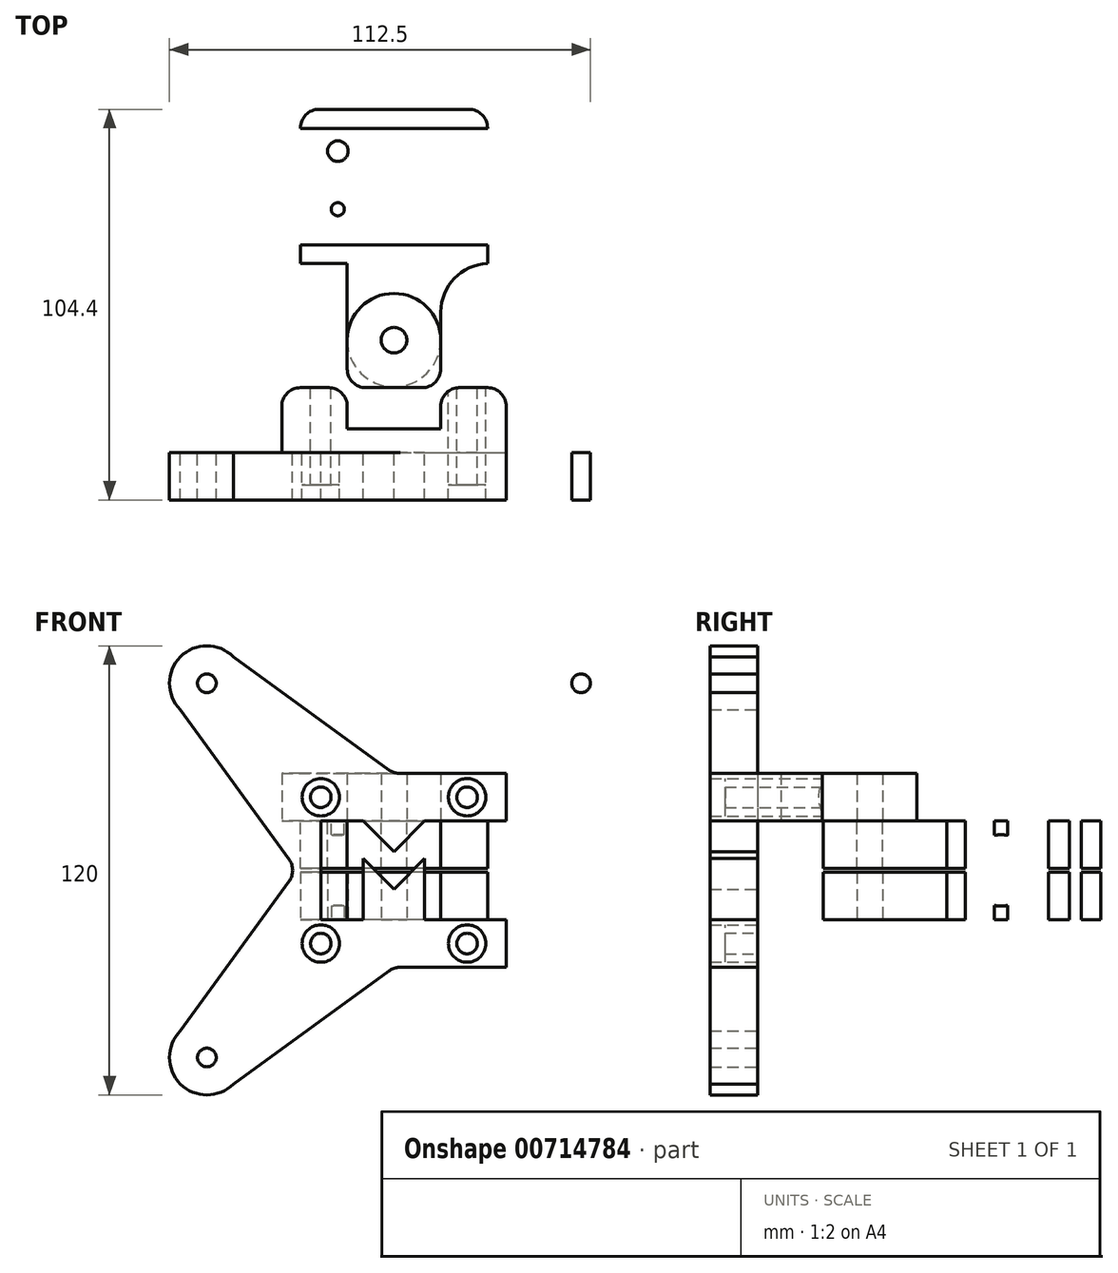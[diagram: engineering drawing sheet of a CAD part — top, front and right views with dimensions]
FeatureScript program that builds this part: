
annotation { "Feature Type Name" : "Feature", "Feature Type Description" : "" }
export const myFeature = defineFeature(function(context is Context, id is Id, definition is map)
    precondition{}
    {
        {
            assignVariable(context, id + "F0", {"name" : "sheet_thickness", "anyValue" : 12.7});
        }
        {
            var Q0;
            Q0=qCreatedBy(makeId("Front.planeOp"),FACE);
            var sketch = newSketch(context, id + "F1", { "sketchPlane" : qUnion([Q0])});
            skLineSegment(sketch, "E0.bottom", {"start": v(60, 60) * mm, "end": v(-60, 60) * mm});
            skLineSegment(sketch, "E0.top", {"start": v(60, -60) * mm, "end": v(-60, -60) * mm});
            skLineSegment(sketch, "E0.left", {"start": v(60, 60) * mm, "end": v(60, -60) * mm});
            skLineSegment(sketch, "E0.right", {"start": v(-60, 60) * mm, "end": v(-60, -60) * mm});
            skPoint(sketch, "E0.middle", {"position": v(0, 0) * mm});
            skCircle(sketch, "E1", {"center": v(-50, 50) * mm, "radius": 2.5 * mm});
            skLineSegment(sketch, "E2", {"start": v(0, 0) * mm, "end": v(0, 60) * mm, "construction": true});
            skPoint(sketch, "E2.endSnap0", {"position": v(0, 60) * mm});
            skLineSegment(sketch, "E3", {"start": v(0, 0) * mm, "end": v(60, 0) * mm, "construction": true});
            skPoint(sketch, "E3.endSnap0", {"position": v(60, 0) * mm});
            skCircle(sketch, "E4.MirrorC", {"center": v(50, 50) * mm, "radius": 2.5 * mm});
            skCircle(sketch, "E5.MirrorC", {"center": v(50, -50) * mm, "radius": 2.5 * mm});
            skCircle(sketch, "E6.MirrorC", {"center": v(-50, -50) * mm, "radius": 2.5 * mm});
            skLineSegment(sketch, "E7.bottom", {"start": v(-30, 25.9) * mm, "end": v(30, 25.9) * mm});
            skLineSegment(sketch, "E7.top", {"start": v(-30, 13.2) * mm, "end": v(30, 13.2) * mm});
            skLineSegment(sketch, "E7.left", {"start": v(-30, 25.9) * mm, "end": v(-30, 13.2) * mm});
            skLineSegment(sketch, "E7.right", {"start": v(30, 25.9) * mm, "end": v(30, 13.2) * mm});
            skLineSegment(sketch, "E8.MirrorCS", {"start": v(30, -25.9) * mm, "end": v(30, -13.2) * mm});
            skLineSegment(sketch, "E9.MirrorCS", {"start": v(-30, -13.2) * mm, "end": v(30, -13.2) * mm});
            skLineSegment(sketch, "E10.MirrorCS", {"start": v(-30, -25.9) * mm, "end": v(-30, -13.2) * mm});
            skLineSegment(sketch, "E11.MirrorCS", {"start": v(-30, -25.9) * mm, "end": v(30, -25.9) * mm});
            skLineSegment(sketch, "E12", {"start": v(-30, 19.55) * mm, "end": v(30, 19.55) * mm, "construction": true});
            skCircle(sketch, "E13", {"center": v(-19.55, 19.55) * mm, "radius": 2.75 * mm});
            skCircle(sketch, "E14.MirrorC", {"center": v(19.55, 19.55) * mm, "radius": 2.75 * mm});
            skCircle(sketch, "E15.MirrorC", {"center": v(19.55, -19.55) * mm, "radius": 2.75 * mm});
            skCircle(sketch, "E16.MirrorC", {"center": v(-19.55, -19.55) * mm, "radius": 2.75 * mm});
            skArc(sketch, "E17", {"start": v(57.07, 42.93) * mm, "mid": v(57.07, 57.07) * mm, "end": v(42.93, 57.07) * mm});
            skLineSegment(sketch, "E18", {"start": v(57.07, 42.93) * mm, "end": v(25.9, 0) * mm});
            skLineSegment(sketch, "E19", {"start": v(0, 0) * mm, "end": v(50, 50) * mm, "construction": true});
            skLineSegment(sketch, "E20", {"start": v(57.07, 42.93) * mm, "end": v(42.93, 57.07) * mm, "construction": true});
            skLineSegment(sketch, "E21.MirrorCS", {"start": v(42.93, 57.07) * mm, "end": v(0, 25.9) * mm});
            skLineSegment(sketch, "E22.MirrorCS", {"start": v(-42.93, 57.07) * mm, "end": v(0, 25.9) * mm});
            skLineSegment(sketch, "E23.MirrorCS", {"start": v(-57.07, 42.93) * mm, "end": v(-25.9, 0) * mm});
            skArc(sketch, "E24.MirrorCS", {"start": v(-57.07, 42.93) * mm, "mid": v(-57.07, 57.07) * mm, "end": v(-42.93, 57.07) * mm});
            skLineSegment(sketch, "E25.MirrorCS", {"start": v(57.07, -42.93) * mm, "end": v(25.9, 0) * mm});
            skArc(sketch, "E26.MirrorCS", {"start": v(57.07, -42.93) * mm, "mid": v(57.07, -57.07) * mm, "end": v(42.93, -57.07) * mm});
            skLineSegment(sketch, "E27.MirrorCS", {"start": v(42.93, -57.07) * mm, "end": v(0, -25.9) * mm});
            skLineSegment(sketch, "E28.MirrorCS", {"start": v(-42.93, -57.07) * mm, "end": v(0, -25.9) * mm});
            skArc(sketch, "E29.MirrorCS", {"start": v(-57.07, -42.93) * mm, "mid": v(-57.07, -57.07) * mm, "end": v(-42.93, -57.07) * mm});
            skLineSegment(sketch, "E30.MirrorCS", {"start": v(-57.07, -42.93) * mm, "end": v(-25.9, 0) * mm});
            skLineSegment(sketch, "E31", {"start": v(19.55, -13.2) * mm, "end": v(19.55, 13.2) * mm});
            skLineSegment(sketch, "E32", {"start": v(19.55, 13.2) * mm, "end": v(8.2, 13.2) * mm});
            skLineSegment(sketch, "E33", {"start": v(8.2, 13.2) * mm, "end": v(0, 5) * mm});
            skLineSegment(sketch, "E34", {"start": v(8.2, -13.2) * mm, "end": v(8.2, 3.2) * mm});
            skLineSegment(sketch, "E35", {"start": v(8.2, 3.2) * mm, "end": v(0, -5) * mm});
            skLineSegment(sketch, "E36.MirrorCS", {"start": v(-8.2, 3.2) * mm, "end": v(0, -5) * mm});
            skLineSegment(sketch, "E37.MirrorCS", {"start": v(-8.2, 13.2) * mm, "end": v(0, 5) * mm});
            skLineSegment(sketch, "E38.MirrorCS", {"start": v(-8.2, -13.2) * mm, "end": v(-8.2, 3.2) * mm});
            skLineSegment(sketch, "E39.MirrorCS", {"start": v(-19.55, -13.2) * mm, "end": v(-19.55, 13.2) * mm});
            skCircle(sketch, "E40", {"center": v(-19.55, 19.55) * mm, "radius": 5 * mm});
            skCircle(sketch, "E41", {"center": v(19.55, 19.55) * mm, "radius": 5 * mm});
            skCircle(sketch, "E42", {"center": v(19.55, -19.55) * mm, "radius": 5 * mm});
            skCircle(sketch, "E43", {"center": v(-19.55, -19.55) * mm, "radius": 5 * mm});
            skSolve(sketch);
        }
        {
            var Q0;
            Q0=makeQuery(id+"F1.imprint","IMPRINT",FACE,{"disambiguationData":[TD([[makeQuery(id+"F1.imprint","IMPRINT",EDGE,{"derivedFrom":sQuery(id+"F1.wireOp",EDGE,"E7.bottom")}),-1.0]])]});
            var Q1;
            Q1=makeQuery(id+"F1.imprint","IMPRINT",FACE,{"disambiguationData":[TD([[makeQuery(id+"F1.imprint","IMPRINT",EDGE,{"derivedFrom":sQuery(id+"F1.wireOp",EDGE,"E8.MirrorCS")}),1.0]])]});
            var Q2;
            Q2=makeQuery(id+"F1.imprint","IMPRINT",FACE,{"disambiguationData":[TD([[makeQuery(id+"F1.imprint","IMPRINT",EDGE,{"derivedFrom":sQuery(id+"F1.wireOp",EDGE,"E1")}),-1.0]])]});
            var Q3;
            {var subQ0=sQuery(id+"F1.wireOp",EDGE,"E34");Q3=makeQuery(id+"F1.imprint","IMPRINT",FACE,{"disambiguationData":[TD([[makeQuery(id+"F1.imprint","IMPRINT",EDGE,{"derivedFrom":subQ0}),1.0]])]});}
            var Q4;
            Q4=makeQuery(id+"F1.imprint","IMPRINT",FACE,{"disambiguationData":[TD([[makeQuery(id+"F1.imprint","IMPRINT",EDGE,{"derivedFrom":sQuery(id+"F1.wireOp",EDGE,"E4.MirrorC")}),1.0]])]});
            var Q5;
            {var subQ0=sQuery(id+"F1.wireOp",EDGE,"E33");Q5=makeQuery(id+"F1.imprint","IMPRINT",FACE,{"disambiguationData":[TD([[makeQuery(id+"F1.imprint","IMPRINT",EDGE,{"derivedFrom":subQ0}),-1.0]])]});}
            extrude(context, id + "F2", {"entities" : qUnion([Q0, Q1, Q2, Q3, Q4, Q5]), "depth" : (getVariable(context, 'sheet_thickness')) * mm, "offsetDistance" : 25 * mm});
        }
        {
            var Q0;
            Q0=makeQuery(id+"F1.imprint","IMPRINT",FACE,{"disambiguationData":[TD([[makeQuery(id+"F1.imprint","IMPRINT",EDGE,{"derivedFrom":sQuery(id+"F1.wireOp",EDGE,"E14.MirrorC")}),1.0]])]});
            var Q1;
            Q1=makeQuery(id+"F1.imprint","IMPRINT",FACE,{"disambiguationData":[TD([[makeQuery(id+"F1.imprint","IMPRINT",EDGE,{"derivedFrom":sQuery(id+"F1.wireOp",EDGE,"E13")}),-1.0]])]});
            var Q2;
            Q2=makeQuery(id+"F1.imprint","IMPRINT",FACE,{"disambiguationData":[TD([[makeQuery(id+"F1.imprint","IMPRINT",EDGE,{"derivedFrom":sQuery(id+"F1.wireOp",EDGE,"E15.MirrorC")}),-1.0]])]});
            var Q3;
            Q3=makeQuery(id+"F1.imprint","IMPRINT",FACE,{"disambiguationData":[TD([[makeQuery(id+"F1.imprint","IMPRINT",EDGE,{"derivedFrom":sQuery(id+"F1.wireOp",EDGE,"E16.MirrorC")}),1.0]])]});
            var Q4;
            Q4=makeQuery(id+"F2.opExtrude","CAP_FACE",FACE,{"disambiguationData":[OSD([sQuery(id+"F1.wireOp",EDGE,"E1"),sQuery(id+"F1.wireOp",EDGE,"E4.MirrorC"),sQuery(id+"F1.wireOp",EDGE,"E5.MirrorC"),sQuery(id+"F1.wireOp",EDGE,"E6.MirrorC"),sQuery(id+"F1.wireOp",EDGE,"E7.top"),sQuery(id+"F1.wireOp",EDGE,"E9.MirrorCS"),sQuery(id+"F1.wireOp",EDGE,"E17"),sQuery(id+"F1.wireOp",EDGE,"E18"),sQuery(id+"F1.wireOp",EDGE,"E21.MirrorCS"),sQuery(id+"F1.wireOp",EDGE,"E22.MirrorCS"),sQuery(id+"F1.wireOp",EDGE,"E23.MirrorCS"),sQuery(id+"F1.wireOp",EDGE,"E24.MirrorCS"),sQuery(id+"F1.wireOp",EDGE,"E25.MirrorCS"),sQuery(id+"F1.wireOp",EDGE,"E26.MirrorCS"),sQuery(id+"F1.wireOp",EDGE,"E27.MirrorCS"),sQuery(id+"F1.wireOp",EDGE,"E28.MirrorCS"),sQuery(id+"F1.wireOp",EDGE,"E29.MirrorCS"),sQuery(id+"F1.wireOp",EDGE,"E30.MirrorCS"),sQuery(id+"F1.wireOp",EDGE,"E31"),sQuery(id+"F1.wireOp",EDGE,"E32"),sQuery(id+"F1.wireOp",EDGE,"E33"),sQuery(id+"F1.wireOp",EDGE,"E34"),sQuery(id+"F1.wireOp",EDGE,"E35"),sQuery(id+"F1.wireOp",EDGE,"E36.MirrorCS"),sQuery(id+"F1.wireOp",EDGE,"E37.MirrorCS"),sQuery(id+"F1.wireOp",EDGE,"E38.MirrorCS"),sQuery(id+"F1.wireOp",EDGE,"E39.MirrorCS"),sQuery(id+"F1.wireOp",EDGE,"E40"),sQuery(id+"F1.wireOp",EDGE,"E41"),sQuery(id+"F1.wireOp",EDGE,"E42"),sQuery(id+"F1.wireOp",EDGE,"E43")])],"isStart":false});
            extrude(context, id + "F3", {"entities" : qUnion([Q0, Q1, Q2, Q3]), "operationType" : NewBodyOperationType.ADD, "endBound" : BoundingType.UP_TO_SURFACE, "depth" : (12.5 - 4) * mm, "endBoundEntityFace" : qUnion([Q4]), "hasOffset" : true, "offsetDistance" : 4 * mm});
        }
        {
            var Q0;
            Q0=makeQuery(id+"F2.opExtrude","SWEPT_EDGE",EDGE,{"disambiguationData":[OSD([sQuery(id+"F1.wireOp",EDGE,"E7.bottom"),sQuery(id+"F1.wireOp",EDGE,"E21.MirrorCS"),sQuery(id+"F1.wireOp",EDGE,"E22.MirrorCS")])]});
            var Q1;
            Q1=makeQuery(id+"F2.opExtrude","SWEPT_EDGE",EDGE,{"disambiguationData":[OSD([sQuery(id+"F1.wireOp",EDGE,"E18"),sQuery(id+"F1.wireOp",EDGE,"E25.MirrorCS")])]});
            var Q2;
            Q2=makeQuery(id+"F2.opExtrude","SWEPT_EDGE",EDGE,{"disambiguationData":[OSD([sQuery(id+"F1.wireOp",EDGE,"E11.MirrorCS"),sQuery(id+"F1.wireOp",EDGE,"E27.MirrorCS"),sQuery(id+"F1.wireOp",EDGE,"E28.MirrorCS")])]});
            var Q3;
            Q3=makeQuery(id+"F2.opExtrude","SWEPT_EDGE",EDGE,{"disambiguationData":[OSD([sQuery(id+"F1.wireOp",EDGE,"E23.MirrorCS"),sQuery(id+"F1.wireOp",EDGE,"E30.MirrorCS")])]});
            fillet(context, id + "F4", {"entities" : qUnion([Q0, Q1, Q2, Q3]), "radius" : 5 * mm, "tangentPropagation" : true, "allowEdgeOverflow" : false});
        }
        {
            var Q0;
            Q0=makeQuery(id+"F1.imprint","IMPRINT",FACE,{"disambiguationData":[TD([[makeQuery(id+"F1.imprint","IMPRINT",EDGE,{"derivedFrom":sQuery(id+"F1.wireOp",EDGE,"E7.bottom")}),-1.0]])]});
            var Q1;
            Q1=makeQuery(id+"F1.imprint","IMPRINT",FACE,{"disambiguationData":[TD([[makeQuery(id+"F1.imprint","IMPRINT",EDGE,{"derivedFrom":sQuery(id+"F1.wireOp",EDGE,"E14.MirrorC")}),1.0]])]});
            var Q2;
            Q2=makeQuery(id+"F1.imprint","IMPRINT",FACE,{"disambiguationData":[TD([[makeQuery(id+"F1.imprint","IMPRINT",EDGE,{"derivedFrom":sQuery(id+"F1.wireOp",EDGE,"E13")}),-1.0]])]});
            extrude(context, id + "F5", {"entities" : qUnion([Q0, Q1, Q2]), "oppositeDirection" : true, "depth" : 6.25 * mm, "offsetDistance" : 25 * mm});
        }
        {
            var Q0;
            Q0=makeQuery(id+"F5.opExtrude","SWEPT_FACE",FACE,{"disambiguationData":[OSD([sQuery(id+"F1.wireOp",EDGE,"E7.top")])]});
            var sketch = newSketch(context, id + "F6", { "sketchPlane" : qUnion([Q0])});
            skLineSegment(sketch, "E44", {"start": v(0, 0) * mm, "end": v(0, -102.76) * mm, "construction": true});
            skCircle(sketch, "E45", {"center": v(0, -30) * mm, "radius": 3.43 * mm});
            skCircle(sketch, "E46", {"center": v(0, -30) * mm, "radius": 4.76 * mm, "construction": true});
            skLineSegment(sketch, "E47.bottom", {"start": v(-12.5, -6.25) * mm, "end": v(12.5, -6.25) * mm});
            skLineSegment(sketch, "E47.top", {"start": v(-12.5, -42.5) * mm, "end": v(12.5, -42.5) * mm});
            skLineSegment(sketch, "E47.left", {"start": v(-12.5, -6.25) * mm, "end": v(-12.5, -42.5) * mm});
            skLineSegment(sketch, "E47.right", {"start": v(12.5, -6.25) * mm, "end": v(12.5, -42.5) * mm});
            skCircle(sketch, "E48", {"center": v(0, -30) * mm, "radius": 12.5 * mm});
            skLineSegment(sketch, "E49", {"start": v(0, -30) * mm, "end": v(12.5, -30) * mm, "construction": true});
            skLineSegment(sketch, "E50", {"start": v(12.5, -42.5) * mm, "end": v(12.5, -50.48) * mm});
            skLineSegment(sketch, "E51", {"start": v(12.5, -50.48) * mm, "end": v(-12.5, -50.48) * mm});
            skLineSegment(sketch, "E52", {"start": v(-12.5, -50.48) * mm, "end": v(-12.5, -42.5) * mm});
            skLineSegment(sketch, "E53", {"start": v(-30, -6.25) * mm, "end": v(-30, -17.3) * mm});
            skLineSegment(sketch, "E54", {"start": v(-30, -17.3) * mm, "end": v(-12.5, -17.3) * mm});
            skLineSegment(sketch, "E55", {"start": v(-12.5, -17.3) * mm, "end": v(12.5, -17.3) * mm});
            skLineSegment(sketch, "E56", {"start": v(12.5, -17.3) * mm, "end": v(30, -17.3) * mm});
            skLineSegment(sketch, "E57", {"start": v(30, -17.3) * mm, "end": v(30, -6.25) * mm});
            skLineSegment(sketch, "E58.bottom", {"start": v(30, -55.47) * mm, "end": v(-30, -55.47) * mm});
            skLineSegment(sketch, "E58.top", {"start": v(30, -74.52) * mm, "end": v(-30, -74.52) * mm});
            skLineSegment(sketch, "E58.left", {"start": v(30, -55.47) * mm, "end": v(30, -74.52) * mm});
            skLineSegment(sketch, "E58.right", {"start": v(-30, -55.47) * mm, "end": v(-30, -74.52) * mm});
            skPoint(sketch, "E58.middle", {"position": v(0, -65) * mm});
            skLineSegment(sketch, "E59", {"start": v(-12.5, -50.48) * mm, "end": v(-30, -50.48) * mm});
            skLineSegment(sketch, "E60", {"start": v(-30, -50.48) * mm, "end": v(-30, -55.47) * mm});
            skLineSegment(sketch, "E61", {"start": v(12.5, -50.48) * mm, "end": v(30, -50.47) * mm});
            skLineSegment(sketch, "E62", {"start": v(30, -50.47) * mm, "end": v(30, -55.47) * mm});
            skLineSegment(sketch, "E63", {"start": v(-30, -74.52) * mm, "end": v(-30, -86.52) * mm});
            skLineSegment(sketch, "E64", {"start": v(-30, -86.52) * mm, "end": v(30, -86.52) * mm});
            skLineSegment(sketch, "E65", {"start": v(30, -86.53) * mm, "end": v(30, -74.52) * mm});
            skCircle(sketch, "E66", {"center": v(15, -65) * mm, "radius": 1.75 * mm});
            skCircle(sketch, "E67", {"center": v(15, -80.53) * mm, "radius": 2.75 * mm});
            skLineSegment(sketch, "E68", {"start": v(30, -80.53) * mm, "end": v(0, -80.53) * mm, "construction": true});
            skCircle(sketch, "E69.MirrorC", {"center": v(-15, -65) * mm, "radius": 1.75 * mm});
            skCircle(sketch, "E70.MirrorC", {"center": v(-15, -80.53) * mm, "radius": 2.75 * mm});
            skLineSegment(sketch, "E71.0", {"start": v(42.93, 12.7) * mm, "end": v(2.94, 12.7) * mm});
            skLineSegment(sketch, "E72", {"start": v(0, 12.7) * mm, "end": v(279.4, 12.7) * mm, "construction": true});
            skLineSegment(sketch, "E73", {"start": v(0, -65) * mm, "end": v(279.4, 12.7) * mm, "construction": true});
            skSolve(sketch);
        }
        {
            var Q0;
            {var subQ0=sQuery(id+"F6.wireOp",EDGE,"E47.bottom");Q0=makeQuery(id+"F6.imprint","IMPRINT",FACE,{"disambiguationData":[TD([[makeQuery(id+"F6.imprint","IMPRINT",EDGE,{"derivedFrom":subQ0}),1.0]])]});}
            var Q1;
            Q1=makeQuery(id+"F6.imprint","IMPRINT",FACE,{"disambiguationData":[TD([[makeQuery(id+"F6.imprint","IMPRINT",EDGE,{"derivedFrom":sQuery(id+"F6.wireOp",EDGE,"E45")}),-1.0]])]});
            var Q2;
            {var subQ0=sQuery(id+"F6.wireOp",EDGE,"E55");Q2=makeQuery(id+"F6.imprint","IMPRINT",FACE,{"disambiguationData":[TD([[makeQuery(id+"F6.imprint","IMPRINT",EDGE,{"derivedFrom":subQ0}),-1.0]])]});}
            var Q3;
            {var subQ5=sQuery(id+"F6.wireOp",EDGE,"E53");Q3=makeQuery(id+"F6.imprint","IMPRINT",FACE,{"disambiguationData":[TD([[makeQuery(id+"F6.imprint","IMPRINT",EDGE,{"derivedFrom":subQ5}),1.0]])]});}
            var Q4;
            {var subQ4=sQuery(id+"F6.wireOp",EDGE,"E56");Q4=makeQuery(id+"F6.imprint","IMPRINT",FACE,{"disambiguationData":[TD([[makeQuery(id+"F6.imprint","IMPRINT",EDGE,{"derivedFrom":subQ4}),1.0]])]});}
            var Q5;
            Q5=makeQuery(id+"F5.opExtrude","SWEPT_FACE",FACE,{"disambiguationData":[OSD([sQuery(id+"F1.wireOp",EDGE,"E7.bottom")])]});
            extrude(context, id + "F7", {"entities" : qUnion([Q0, Q1, Q2, Q3, Q4]), "operationType" : NewBodyOperationType.ADD, "endBound" : BoundingType.UP_TO_SURFACE, "oppositeDirection" : true, "depth" : 10 * mm, "endBoundEntityFace" : qUnion([Q5]), "offsetDistance" : 25 * mm});
        }
        {
            var Q0;
            Q0=makeQuery(id+"F6.imprint","IMPRINT",FACE,{"disambiguationData":[TD([[makeQuery(id+"F6.imprint","IMPRINT",EDGE,{"derivedFrom":sQuery(id+"F6.wireOp",EDGE,"E45")}),-1.0]])]});
            var Q1;
            {var subQ0=sQuery(id+"F6.wireOp",EDGE,"E47.left");var subQ3=sQuery(id+"F6.wireOp",EDGE,"E48");var subQ5=makeQuery(id+"F6.imprint","INTERSECT",VERTEX,{"derivedFrom":[subQ0,subQ3]});Q1=makeQuery(id+"F6.imprint","IMPRINT",FACE,{"disambiguationData":[TD([[makeQuery(id+"F6.imprint","IMPRINT",EDGE,{"disambiguationData":[TD([[subQ5,-1.0]])],"derivedFrom":subQ3}),-1.0]])]});}
            var Q2;
            {var subQ0=sQuery(id+"F6.wireOp",EDGE,"E50");Q2=makeQuery(id+"F6.imprint","IMPRINT",FACE,{"disambiguationData":[TD([[makeQuery(id+"F6.imprint","IMPRINT",EDGE,{"derivedFrom":subQ0}),-1.0]])]});}
            var Q3;
            {var subQ0=sQuery(id+"F6.wireOp",EDGE,"E47.right");var subQ3=sQuery(id+"F6.wireOp",EDGE,"E48");var subQ5=makeQuery(id+"F6.imprint","INTERSECT",VERTEX,{"derivedFrom":[subQ0,subQ3]});Q3=makeQuery(id+"F6.imprint","IMPRINT",FACE,{"disambiguationData":[TD([[makeQuery(id+"F6.imprint","IMPRINT",EDGE,{"disambiguationData":[TD([[subQ5,1.0]])],"derivedFrom":subQ3}),-1.0]])]});}
            extrude(context, id + "F8", {"entities" : qUnion([Q0, Q1, Q2, Q3]), "depth" : (getVariable(context, 'sheet_thickness')) * mm, "offsetDistance" : 25 * mm});
        }
        {
            var Q0;
            Q0=qCreatedBy(makeId("Right.planeOp"),FACE);
            var sketch = newSketch(context, id + "F9", { "sketchPlane" : qUnion([Q0])});
            skLineSegment(sketch, "E74", {"start": v(0, 0) * mm, "end": v(91.7, 0) * mm, "construction": true});
            skCircle(sketch, "E75", {"center": v(64.99, 0) * mm, "radius": 9.53 * mm});
            skCircle(sketch, "E76", {"center": v(64.99, 0) * mm, "radius": 13.2 * mm});
            skLineSegment(sketch, "E77", {"start": v(91.7, 0.5) * mm, "end": v(91.7, 13.2) * mm});
            skLineSegment(sketch, "E78.bottom", {"start": v(80.18, 15.2) * mm, "end": v(89.7, 15.2) * mm, "construction": true});
            skLineSegment(sketch, "E78.top", {"start": v(80.18, 13.2) * mm, "end": v(89.7, 13.2) * mm, "construction": true});
            skLineSegment(sketch, "E78.left", {"start": v(80.18, 13.2) * mm, "end": v(80.18, 15.2) * mm, "construction": true});
            skLineSegment(sketch, "E78.right", {"start": v(89.7, 13.2) * mm, "end": v(89.7, 15.2) * mm, "construction": true});
            skLineSegment(sketch, "E79", {"start": v(91.7, 0.5) * mm, "end": v(0, 0.5) * mm});
            skLineSegment(sketch, "E80", {"start": v(0, 0.5) * mm, "end": v(0, 0) * mm});
            skLineSegment(sketch, "E81.0", {"start": v(30, 13.2) * mm, "end": v(50.48, 13.2) * mm});
            skLineSegment(sketch, "E82", {"start": v(50.48, 13.2) * mm, "end": v(91.7, 13.2) * mm});
            skLineSegment(sketch, "E83.0", {"start": v(50.48, 0.5) * mm, "end": v(50.48, 13.2) * mm});
            skPoint(sketch, "E84", {"position": v(55.47, 0.5) * mm});
            skPoint(sketch, "E85", {"position": v(78.18, 0.5) * mm});
            skSolve(sketch);
        }
        {
            var Q0;
            {var subQ0=sQuery(id+"F9.wireOp",EDGE,"E82");var subQ1=sQuery(id+"F9.wireOp",EDGE,"E76");var subQ2=makeQuery(id+"F9.imprint","INTERSECT",VERTEX,{"derivedFrom":[subQ1,subQ0]});Q0=makeQuery(id+"F9.imprint","IMPRINT",FACE,{"disambiguationData":[TD([[makeQuery(id+"F9.imprint","IMPRINT",EDGE,{"disambiguationData":[TD([[subQ2,-1.0]])],"derivedFrom":subQ1}),-1.0]])]});}
            var Q1;
            {var subQ0=sQuery(id+"F9.wireOp",EDGE,"E76");var subQ8=makeQuery(id+"F9.imprint","INTERSECT",VERTEX,{"derivedFrom":[subQ0,sQuery(id+"F9.wireOp",EDGE,"HIz0KHZZ-02JB-yLJv-mDsw-wXDEuecVXzhu")]});Q1=makeQuery(id+"F9.imprint","IMPRINT",FACE,{"disambiguationData":[TD([[makeQuery(id+"F9.imprint","IMPRINT",EDGE,{"disambiguationData":[TD([[subQ8,1.0]])],"derivedFrom":subQ0}),1.0]])]});}
            var Q2;
            {var subQ0=sQuery(id+"F9.wireOp",EDGE,"HIz0KHZZ-02JB-yLJv-mDsw-wXDEuecVXzhu");Q2=makeQuery(id+"F9.imprint","IMPRINT",FACE,{"disambiguationData":[TD([[makeQuery(id+"F9.imprint","IMPRINT",EDGE,{"derivedFrom":subQ0}),-1.0]])]});}
            var Q3;
            {var subQ0=sQuery(id+"F9.wireOp",EDGE,"HIz0KHZZ-02JB-yLJv-mDsw-wXDEuecVXzhu");Q3=makeQuery(id+"F9.imprint","IMPRINT",FACE,{"disambiguationData":[TD([[makeQuery(id+"F9.imprint","IMPRINT",EDGE,{"derivedFrom":subQ0}),1.0]])]});}
            var Q4;
            {var subQ5=sQuery(id+"F9.wireOp",EDGE,"E77");Q4=makeQuery(id+"F9.imprint","IMPRINT",FACE,{"disambiguationData":[TD([[makeQuery(id+"F9.imprint","IMPRINT",EDGE,{"derivedFrom":subQ5}),1.0]])]});}
            extrude(context, id + "F10", {"entities" : qUnion([Q0, Q1, Q2, Q3, Q4]), "operationType" : NewBodyOperationType.ADD, "endBound" : BoundingType.SYMMETRIC, "depth" : 50 * mm, "offsetDistance" : 25 * mm});
        }
        {
            var Q0;
            Q0=makeQuery(id+"F6.imprint","IMPRINT",FACE,{"disambiguationData":[TD([[makeQuery(id+"F6.imprint","IMPRINT",EDGE,{"derivedFrom":sQuery(id+"F6.wireOp",EDGE,"E69.MirrorC")}),-1.0]])]});
            var Q1;
            Q1=makeQuery(id+"F6.imprint","IMPRINT",FACE,{"disambiguationData":[TD([[makeQuery(id+"F6.imprint","IMPRINT",EDGE,{"derivedFrom":sQuery(id+"F6.wireOp",EDGE,"E66")}),1.0]])]});
            var Q2;
            Q2=makeQuery(id+"F6.imprint","IMPRINT",FACE,{"disambiguationData":[TD([[makeQuery(id+"F6.imprint","IMPRINT",EDGE,{"derivedFrom":sQuery(id+"F6.wireOp",EDGE,"E67")}),1.0]])]});
            var Q3;
            Q3=makeQuery(id+"F6.imprint","IMPRINT",FACE,{"disambiguationData":[TD([[makeQuery(id+"F6.imprint","IMPRINT",EDGE,{"derivedFrom":sQuery(id+"F6.wireOp",EDGE,"E70.MirrorC")}),-1.0]])]});
            extrude(context, id + "F11", {"entities" : qUnion([Q0, Q1, Q2, Q3]), "operationType" : NewBodyOperationType.REMOVE, "depth" : 25 * mm, "offsetDistance" : 25 * mm});
        }
        {
            var Q0;
            Q0=makeQuery(id+"F10.opExtrude","CAP_EDGE",EDGE,{"disambiguationData":[OSD([sQuery(id+"F9.wireOp",EDGE,"E77"),sQuery(id+"F9.wireOp",EDGE,"RPQXRJDk-1qIu-eflv-rFsv-AzynY6bBEAN9")])],"isStart":false});
            var Q1;
            Q1=makeQuery(id+"F10.opExtrude","CAP_EDGE",EDGE,{"disambiguationData":[OSD([sQuery(id+"F9.wireOp",EDGE,"E77"),sQuery(id+"F9.wireOp",EDGE,"RPQXRJDk-1qIu-eflv-rFsv-AzynY6bBEAN9")])],"isStart":true});
            var Q2;
            Q2=makeQuery(id+"F7.opExtrude","SWEPT_EDGE",EDGE,{"disambiguationData":[OSD([sQuery(id+"F6.wireOp",EDGE,"E56"),sQuery(id+"F6.wireOp",EDGE,"E57")])]});
            var Q3;
            Q3=makeQuery(id+"F7.opExtrude","SWEPT_EDGE",EDGE,{"disambiguationData":[OSD([sQuery(id+"F6.wireOp",EDGE,"E47.right"),sQuery(id+"F6.wireOp",EDGE,"E55"),sQuery(id+"F6.wireOp",EDGE,"E56")])]});
            var Q4;
            Q4=makeQuery(id+"F7.opExtrude","SWEPT_EDGE",EDGE,{"disambiguationData":[OSD([sQuery(id+"F6.wireOp",EDGE,"E53"),sQuery(id+"F6.wireOp",EDGE,"E54")])]});
            var Q5;
            Q5=makeQuery(id+"F7.opExtrude","SWEPT_EDGE",EDGE,{"disambiguationData":[OSD([sQuery(id+"F6.wireOp",EDGE,"E47.left"),sQuery(id+"F6.wireOp",EDGE,"E54"),sQuery(id+"F6.wireOp",EDGE,"E55")])]});
            fillet(context, id + "F12", {"entities" : qUnion([Q0, Q1, Q2, Q3, Q4, Q5]), "radius" : 5 * mm, "tangentPropagation" : true, "allowEdgeOverflow" : false});
        }
        {
            var Q0;
            Q0=makeQuery(id+"F8.opExtrude","SWEPT_EDGE",EDGE,{"disambiguationData":[OSD([sQuery(id+"F6.wireOp",EDGE,"E50"),sQuery(id+"F6.wireOp",EDGE,"E51"),sQuery(id+"F6.wireOp",EDGE,"E61")])]});
            var Q1;
            Q1=makeQuery(id+"F8.opExtrude","SWEPT_EDGE",EDGE,{"disambiguationData":[OSD([sQuery(id+"F6.wireOp",EDGE,"E51"),sQuery(id+"F6.wireOp",EDGE,"E52"),sQuery(id+"F6.wireOp",EDGE,"E59")])]});
            fillet(context, id + "F13", {"entities" : qUnion([Q0, Q1]), "radius" : 13 * mm, "tangentPropagation" : true, "allowEdgeOverflow" : false});
        }
        {
            var Q0;
            Q0=makeQuery(id+"F1.imprint","IMPRINT",FACE,{"disambiguationData":[TD([[makeQuery(id+"F1.imprint","IMPRINT",EDGE,{"derivedFrom":sQuery(id+"F1.wireOp",EDGE,"E13")}),1.0]])]});
            var Q1;
            Q1=makeQuery(id+"F1.imprint","IMPRINT",FACE,{"disambiguationData":[TD([[makeQuery(id+"F1.imprint","IMPRINT",EDGE,{"derivedFrom":sQuery(id+"F1.wireOp",EDGE,"E14.MirrorC")}),-1.0]])]});
            extrude(context, id + "F14", {"entities" : qUnion([Q0, Q1]), "operationType" : NewBodyOperationType.REMOVE, "endBound" : BoundingType.THROUGH_ALL, "oppositeDirection" : true, "depth" : 25 * mm, "offsetDistance" : 25 * mm});
        }
        {
            var Q0;
            Q0=makeQuery(id+"F5.opExtrude","SWEPT_BODY",BODY,{"disambiguationData":[OSD([sQuery(id+"F1.wireOp",EDGE,"E7.bottom"),sQuery(id+"F1.wireOp",EDGE,"E7.top"),sQuery(id+"F1.wireOp",EDGE,"E7.left"),sQuery(id+"F1.wireOp",EDGE,"E7.right"),sQuery(id+"F1.wireOp",EDGE,"E13"),sQuery(id+"F1.wireOp",EDGE,"E14.MirrorC")])]});
            var Q1;
            Q1=makeQuery(id+"F8.opExtrude","SWEPT_BODY",BODY,{"disambiguationData":[OSD([sQuery(id+"F6.wireOp",EDGE,"E45"),sQuery(id+"F6.wireOp",EDGE,"E47.left"),sQuery(id+"F6.wireOp",EDGE,"E47.right"),sQuery(id+"F6.wireOp",EDGE,"E48"),sQuery(id+"F6.wireOp",EDGE,"E50"),sQuery(id+"F6.wireOp",EDGE,"E51"),sQuery(id+"F6.wireOp",EDGE,"E52")])]});
            var Q2;
            Q2=qCreatedBy(makeId("Top.planeOp"),FACE);
            mirror(context, id + "F15", {"entities" : qUnion([Q0, Q1]), "mirrorPlane" : qUnion([Q2])});
        }
    });
